# Revit family: ON5UM
name_source: partatom
category: Mechanical Equipment
units: mm (PartAtom-declared; Revit-internal decimal feet)

## family parameters
Always vertical = Yes
Cut with Voids When Loaded = No
OmniClass Number = 23.40.40.11.17
OmniClass Title = Refrigerated Cases
Part Type = Normal
Room Calculation Point = No
Round Connector Dimension = Use Radius
Shared = No
Work Plane-Based = Yes

## types (4) — shared parameters
10" Shelf = Yes
12" Shelf = Yes
14" Shelf = Yes
16" Shelf = Yes
BOTTOM ELECTRICAL = Yes
BOTTOM REFRIGERATION PIPING = Yes
Certifications = NSF 7, UL471, CSA
DATE = 04/01/2016
DRAIN PIPING = Yes
Default Elevation = 48"
Description = Narrow Multi-Deck Merchandiser with Synerg-E™
EQUIPMENT DESCRIPTION = Narrow Multi-Deck Merchandiser with Synerg-E™
EQUIPMENT MARK = ON5UM-NRG
GLASS = Glass
Height = 66 1/4"
How Many Defrosts Per Day = 3
Island Anti-Condensate Heaters Amps = 0 A
Island BTUH Conventional = 1179
Island BTUH Parallel = 1093
Island Discharge Air Velocity (FPM) = 240 FPM
Island Discharge Air(°F) = 31 °F
Island Electric Fail-Safe = 40 (Min)
Island Electric Termination Temp (F°) = 47 °F
Island Evaporator (°F) = 22 °F
Island Hot Gas Fail-Safe (Min) = 26 (Min)
Island Hot Gas Termination Temp (F°) = 45 °F
Island Run-Off Time (Min) = 6-8 (Min)
Island Superheat @ Bulb Set Point (°F) = 6-8 °F
Island Timed-Off Fail-Safe (Min) = 45 (Min)
Island Timed-Off Termination Temp (°F) = 45 °F
Item Description = Narrow Multi-Deck Merchandiser with Synerg-E™
LF STD END = Yes
Legend Number = ON5UM-NRG
Manufacturer = HILL PHOENIX
Model = ON5UM-NRG
PAINTED METAL UPPER SHELF = PAINTED SHELVES
REAR REFRIGERATION PIPING = Yes
REFRIGERATION PIPING = COPPER PIPE
RT STD END = Yes
STAINLESS STEEL = GALVANIZED STEEL
Standard Power Amps = 0 A
TOP ELECTRICAL = Yes
TOP REFRIGERATION PIPING = Yes
URL = http://www.hillphoenix.com
Width = 35 7/8"

## per-type parameters (varying)
| type | DRAIN LINE | High Power (Cornice) Amps | High Power (Cornice) Watts | Island  Case Length | Island 208V Defrost Heaters Amps | Island 208V Defrost Heaters Watts | Island 240 Defrost Heaters Amps | Island 240 Defrost Heaters Watts | Island Anti-Condensate Heaters Watts | Island Fans Per Case | Island High Efficiency Fans Amps | Island High Efficiency Fans Watts | Length | Light Length | Lights Per Row | Refgn | Standard Power Watts |
| 04' | 24" | 0 A | 22 W | 48" | 2 A | 400 A | 2 A | 532 W | 17 W | 2 | 0 A | 28 W | 48" | 48" | 1 | 7 5/8" | 12 W |
| 06' | 36" | 0 A | 30 W | 72" | 3 A | 600 A | 3 A | 798 W | 24 W | 2 | 0 A | 28 W | 72" | 36" | 2 | 8 5/8" | 17 W |
| 08' | 48" | 0 A | 43 W | 96" | 4 A | 800 A | 4 A | 1065 W | 30 W | 3 | 1 A | 42 W | 96" | 48" | 2 | 8 5/8" | 24 W |
| 12' | 72" | 1 A | 65 W | 144" | 6 A | 1200 A | 7 A | 1600 W | 46 W | 4 | 1 A | 52 W | 144" | 48" | 3 | 8 5/8" | 36 W |

## geometry (parser evidence)
native form markers: Blend x9, Sweep x2
no freeform markers — native parametric forms only
